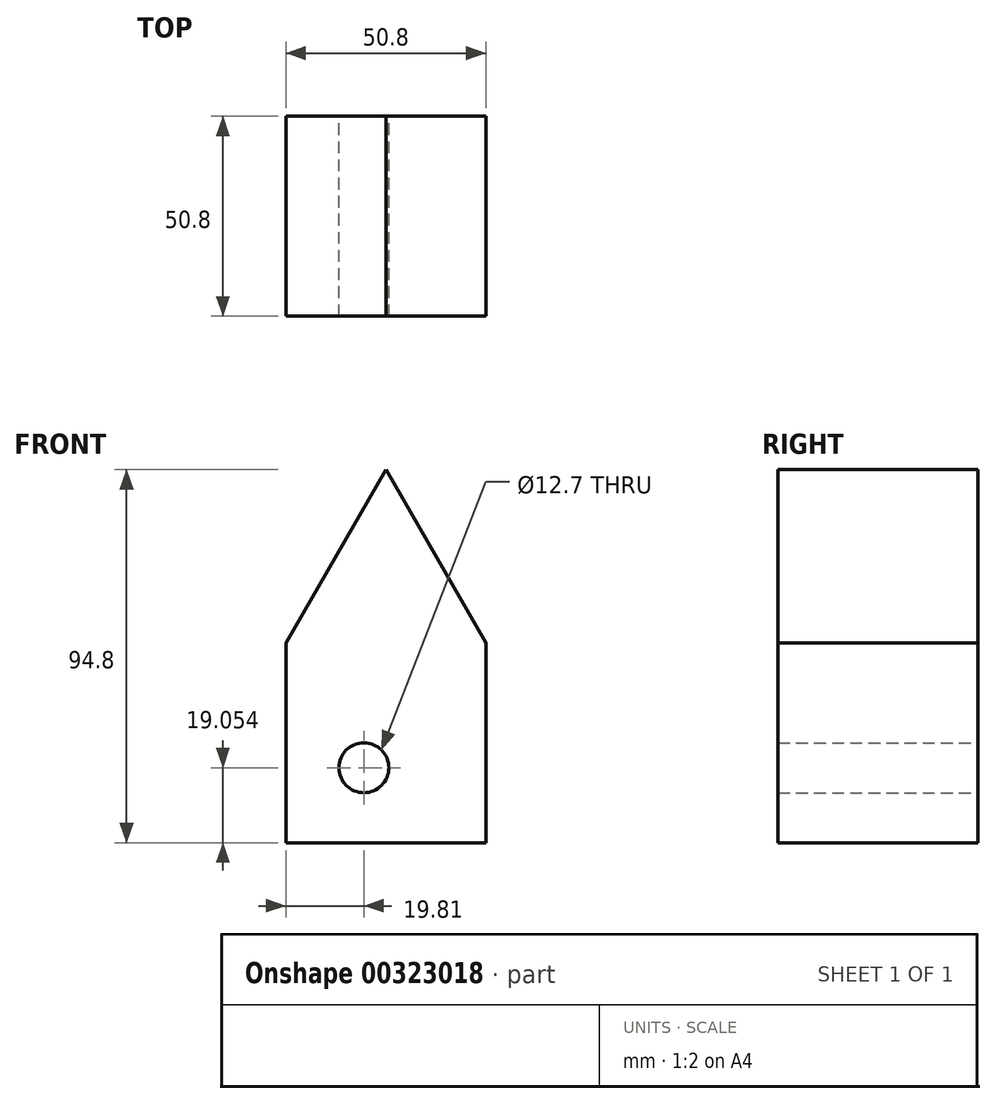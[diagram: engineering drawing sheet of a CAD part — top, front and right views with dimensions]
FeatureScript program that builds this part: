
annotation { "Feature Type Name" : "Feature", "Feature Type Description" : "" }
export const myFeature = defineFeature(function(context is Context, id is Id, definition is map)
    precondition{}
    {
        {
            var Q0;
            Q0=qCreatedBy(makeId("Front.planeOp"),FACE);
            var sketch = newSketch(context, id + "F0", { "sketchPlane" : qUnion([Q0])});
            skLineSegment(sketch, "E0.top", {"start": v(-19.81, -22.6) * mm, "end": v(30.99, -22.6) * mm});
            skLineSegment(sketch, "E0.left", {"start": v(-19.81, 28.2) * mm, "end": v(-19.81, -22.6) * mm});
            skLineSegment(sketch, "E0.right", {"start": v(30.99, 28.2) * mm, "end": v(30.99, -22.6) * mm});
            skLineSegment(sketch, "E1", {"start": v(-19.81, 28.2) * mm, "end": v(5.59, 72.19) * mm});
            skLineSegment(sketch, "E2", {"start": v(5.59, 72.19) * mm, "end": v(30.99, 28.2) * mm});
            skCircle(sketch, "E3", {"center": v(0, -3.56) * mm, "radius": 6.35 * mm});
            skSolve(sketch);
        }
        {
            var Q0;
            Q0 = qSketchRegion(id + "F0", true);
            extrude(context, id + "F1", {"entities" : qUnion([Q0]), "depth" : 50.8 * mm});
        }
    });
